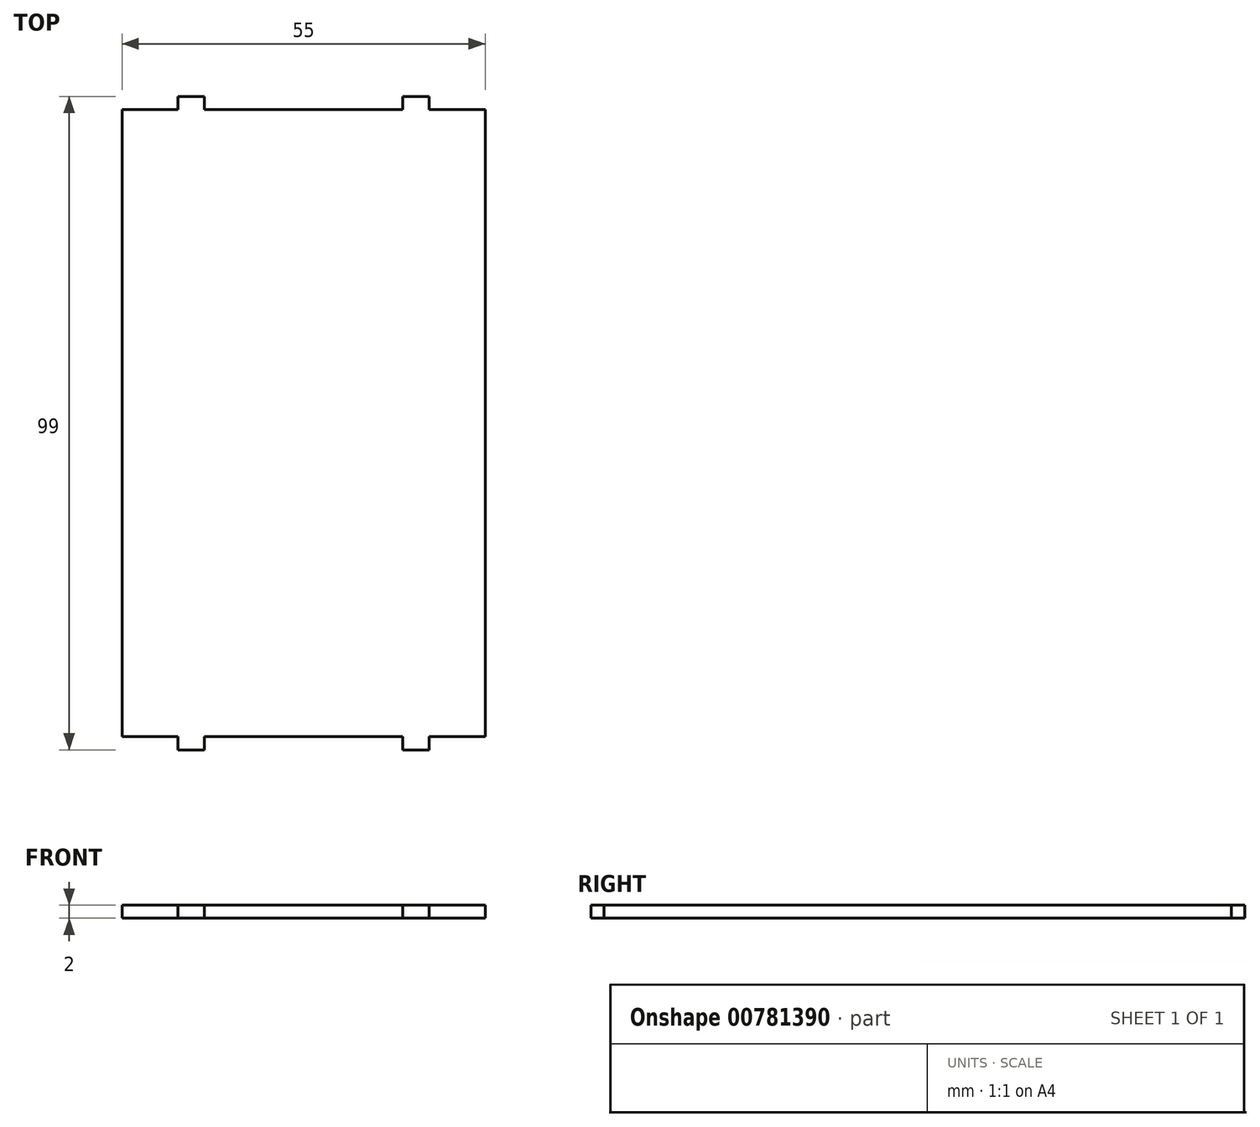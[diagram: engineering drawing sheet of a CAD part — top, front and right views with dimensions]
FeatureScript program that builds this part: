
annotation { "Feature Type Name" : "Feature", "Feature Type Description" : "" }
export const myFeature = defineFeature(function(context is Context, id is Id, definition is map)
    precondition{}
    {
        {
            var Q0;
            Q0=qCreatedBy(makeId("Top.planeOp"),FACE);
            var sketch = newSketch(context, id + "F0", { "sketchPlane" : qUnion([Q0])});
            skLineSegment(sketch, "E0.bottom", {"start": v(27.5, 47.5) * mm, "end": v(-27.5, 47.5) * mm});
            skLineSegment(sketch, "E0.top", {"start": v(27.5, -47.5) * mm, "end": v(-27.5, -47.5) * mm});
            skLineSegment(sketch, "E0.left", {"start": v(27.5, 47.5) * mm, "end": v(27.5, -47.5) * mm});
            skLineSegment(sketch, "E0.right", {"start": v(-27.5, 47.5) * mm, "end": v(-27.5, -47.5) * mm});
            skSolve(sketch);
        }
        {
            var Q0;
            Q0 = qSketchRegion(id + "F0", true);
            extrude(context, id + "F1", {"entities" : qUnion([Q0]), "depth" : 2 * mm, "offsetDistance" : 25 * mm});
        }
        {
            var Q0;
            Q0=makeQuery(id+"F1.opExtrude","SWEPT_FACE",FACE,{"disambiguationData":[OSD([sQuery(id+"F0.wireOp",EDGE,"E0.top")])]});
            var sketch = newSketch(context, id + "F2", { "sketchPlane" : qUnion([Q0])});
            skLineSegment(sketch, "E1.bottom", {"start": v(-15, 0) * mm, "end": v(-19, 0) * mm});
            skLineSegment(sketch, "E1.top", {"start": v(-15, 2) * mm, "end": v(-19, 2) * mm});
            skLineSegment(sketch, "E1.left", {"start": v(-15, 0) * mm, "end": v(-15, 2) * mm});
            skLineSegment(sketch, "E1.right", {"start": v(-19, 0) * mm, "end": v(-19, 2) * mm});
            skLineSegment(sketch, "E2.bottom", {"start": v(15, 0) * mm, "end": v(19, 0) * mm});
            skLineSegment(sketch, "E2.top", {"start": v(15, 2) * mm, "end": v(19, 2) * mm});
            skLineSegment(sketch, "E2.left", {"start": v(15, 0) * mm, "end": v(15, 2) * mm});
            skLineSegment(sketch, "E2.right", {"start": v(19, 0) * mm, "end": v(19, 2) * mm});
            skSolve(sketch);
        }
        {
            var Q0;
            Q0=makeQuery(id+"F2.imprint","IMPRINT",FACE,{"disambiguationData":[TD([[makeQuery(id+"F2.imprint","IMPRINT",EDGE,{"derivedFrom":sQuery(id+"F2.wireOp",EDGE,"E2.bottom")}),-1.0]])]});
            var Q1;
            Q1=makeQuery(id+"F2.imprint","IMPRINT",FACE,{"disambiguationData":[TD([[makeQuery(id+"F2.imprint","IMPRINT",EDGE,{"derivedFrom":sQuery(id+"F2.wireOp",EDGE,"E1.bottom")}),-1.0]])]});
            extrude(context, id + "F3", {"entities" : qUnion([Q0, Q1]), "operationType" : NewBodyOperationType.ADD, "depth" : 2 * mm, "offsetDistance" : 25 * mm});
        }
        {
            var Q0;
            Q0=makeQuery(id+"F1.opExtrude","SWEPT_BODY",BODY,{"disambiguationData":[OSD([sQuery(id+"F0.wireOp",EDGE,"E0.bottom"),sQuery(id+"F0.wireOp",EDGE,"E0.top"),sQuery(id+"F0.wireOp",EDGE,"E0.left"),sQuery(id+"F0.wireOp",EDGE,"E0.right")])]});
            var Q1;
            Q1=qCreatedBy(makeId("Front.planeOp"),FACE);
            mirror(context, id + "F4", {"operationType" : NewBodyOperationType.ADD, "entities" : qUnion([Q0]), "mirrorPlane" : qUnion([Q1])});
        }
    });
